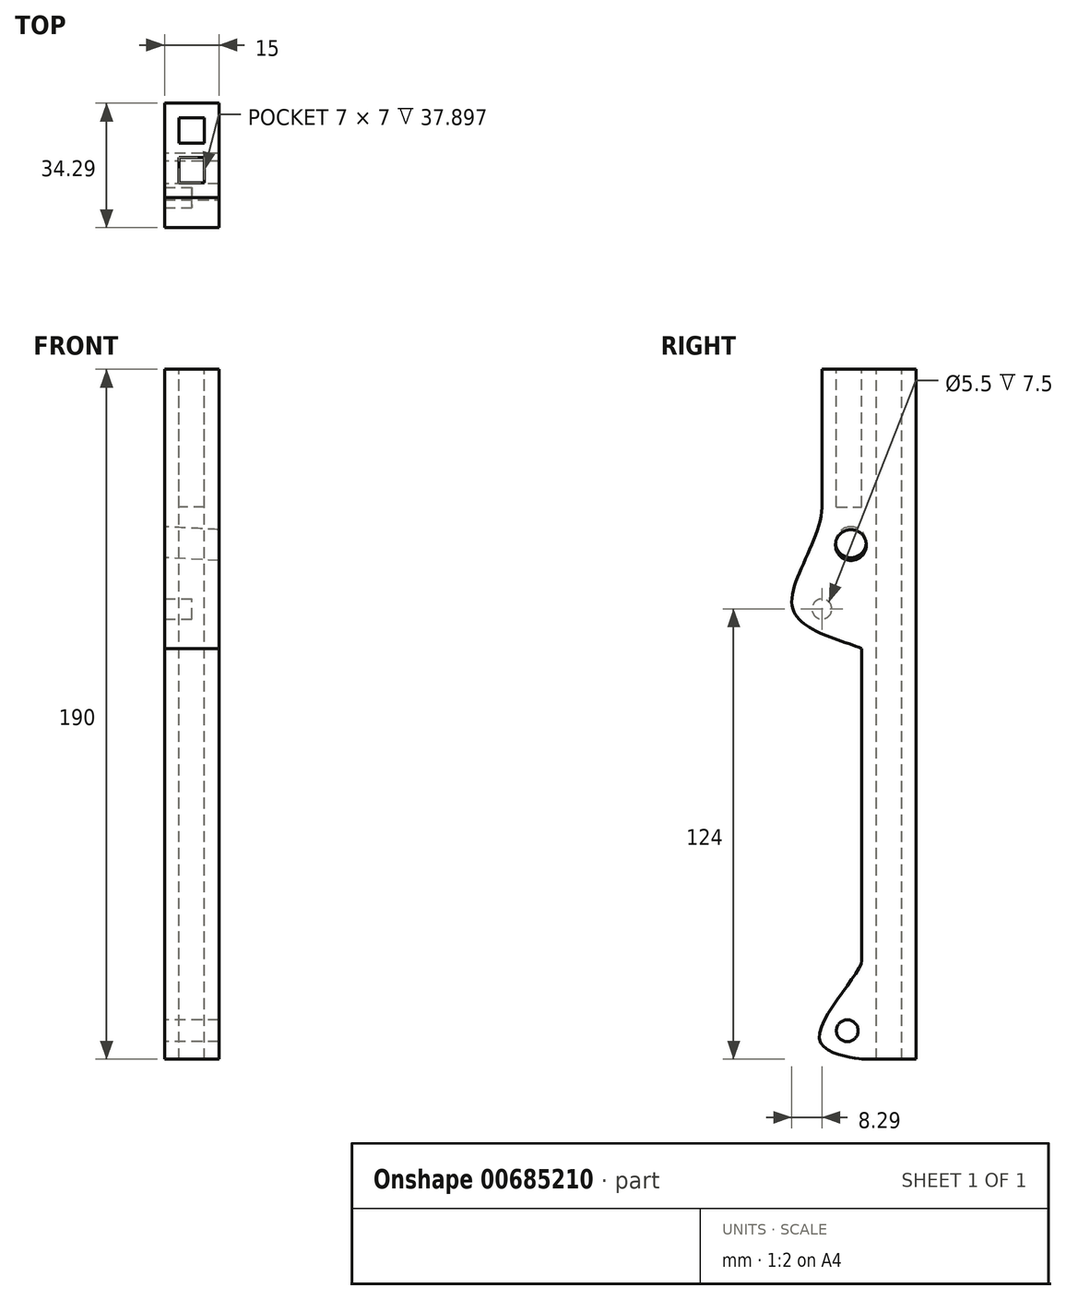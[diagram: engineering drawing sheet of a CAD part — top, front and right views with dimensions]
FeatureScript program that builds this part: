
annotation { "Feature Type Name" : "Feature", "Feature Type Description" : "" }
export const myFeature = defineFeature(function(context is Context, id is Id, definition is map)
    precondition{}
    {
        {
            var Q0;
            Q0=qCreatedBy(makeId("Right.planeOp"),FACE);
            var sketch = newSketch(context, id + "F0", { "sketchPlane" : qUnion([Q0])});
            skLineSegment(sketch, "E0.bottom", {"start": v(7.5, -95) * mm, "end": v(-7.5, -95) * mm});
            skLineSegment(sketch, "E0.top", {"start": v(7.5, 95) * mm, "end": v(-7.5, 95) * mm});
            skLineSegment(sketch, "E0.left", {"start": v(7.5, -95) * mm, "end": v(7.5, 95) * mm});
            skLineSegment(sketch, "E0.right", {"start": v(-7.5, -95) * mm, "end": v(-7.5, 95) * mm});
            skPoint(sketch, "E0.middle", {"position": v(0, 0) * mm});
            skSolve(sketch);
        }
        {
            var Q0;
            Q0=qSketchRegion(id+"F0",true);
            extrude(context, id + "F1", {"entities" : qUnion([Q0]), "endBound" : BoundingType.SYMMETRIC, "depth" : 15 * mm, "offsetDistance" : 25 * mm});
        }
        {
            var Q0;
            Q0=makeQuery(id+"F1.opExtrude","SWEPT_FACE",FACE,{"disambiguationData":[OSD([sQuery(id+"F0.wireOp",EDGE,"E0.top")])]});
            var sketch = newSketch(context, id + "F2", { "sketchPlane" : qUnion([Q0])});
            skLineSegment(sketch, "E1.bottom", {"start": v(3.5, 3.5) * mm, "end": v(-3.5, 3.5) * mm});
            skLineSegment(sketch, "E1.top", {"start": v(3.5, -3.5) * mm, "end": v(-3.5, -3.5) * mm});
            skLineSegment(sketch, "E1.left", {"start": v(3.5, 3.5) * mm, "end": v(3.5, -3.5) * mm});
            skLineSegment(sketch, "E1.right", {"start": v(-3.5, 3.5) * mm, "end": v(-3.5, -3.5) * mm});
            skPoint(sketch, "E1.middle", {"position": v(0, 0) * mm});
            skSolve(sketch);
        }
        {
            var Q0;
            Q0=qSketchRegion(id+"F2",true);
            extrude(context, id + "F3", {"entities" : qUnion([Q0]), "operationType" : NewBodyOperationType.REMOVE, "endBound" : BoundingType.THROUGH_ALL, "oppositeDirection" : true, "depth" : 25 * mm, "offsetDistance" : 25 * mm});
        }
        {
            var Q0;
            Q0=makeQuery(id+"F1.opExtrude","CAP_FACE",FACE,{"disambiguationData":[OSD([sQuery(id+"F0.wireOp",EDGE,"E0.bottom"),sQuery(id+"F0.wireOp",EDGE,"E0.top"),sQuery(id+"F0.wireOp",EDGE,"E0.left"),sQuery(id+"F0.wireOp",EDGE,"E0.right")])],"isStart":false});
            var sketch = newSketch(context, id + "F4", { "sketchPlane" : qUnion([Q0])});
            skLineSegment(sketch, "E2", {"start": v(-7.5, 95) * mm, "end": v(-18.5, 95) * mm});
            skLineSegment(sketch, "E3", {"start": v(-18.5, 95) * mm, "end": v(-18.5, 50) * mm});
            skLineSegment(sketch, "E4", {"start": v(-18.5, 50) * mm, "end": v(-7.5, 50) * mm});
            skSolve(sketch);
        }
        {
            var Q0;
            {var subQ0=sQuery(id+"F4.wireOp",EDGE,"E2");Q0=makeQuery(id+"F4.imprint","IMPRINT",FACE,{"disambiguationData":[TD([[makeQuery(id+"F4.imprint","IMPRINT",EDGE,{"derivedFrom":subQ0}),1.0]])]});}
            extrude(context, id + "F5", {"entities" : qUnion([Q0]), "operationType" : NewBodyOperationType.ADD, "oppositeDirection" : true, "depth" : 15 * mm, "offsetDistance" : 25 * mm});
        }
        {
            var Q0;
            Q0=makeQuery(id+"F5.boolean.opBoolean","MERGE",FACE,{"derivedFrom":[makeQuery(id+"F1.opExtrude","SWEPT_FACE",FACE,{"disambiguationData":[OSD([sQuery(id+"F0.wireOp",EDGE,"E0.top")])]}),makeQuery(id+"F5.opExtrude","SWEPT_FACE",FACE,{"disambiguationData":[OSD([sQuery(id+"F4.wireOp",EDGE,"E2")])]})]});
            var sketch = newSketch(context, id + "F6", { "sketchPlane" : qUnion([Q0])});
            skLineSegment(sketch, "E5", {"start": v(-3.5, -7.5) * mm, "end": v(3.5, -7.5) * mm});
            skLineSegment(sketch, "E6", {"start": v(3.5, -7.5) * mm, "end": v(3.5, -14.5) * mm});
            skLineSegment(sketch, "E7", {"start": v(3.5, -14.5) * mm, "end": v(-3.5, -14.5) * mm});
            skLineSegment(sketch, "E8", {"start": v(-3.5, -14.5) * mm, "end": v(-3.5, -7.5) * mm});
            skSolve(sketch);
        }
        {
            var Q0;
            Q0=makeQuery(id+"F6.imprint","IMPRINT",FACE,{"disambiguationData":[TD([[makeQuery(id+"F6.imprint","IMPRINT",EDGE,{"derivedFrom":sQuery(id+"F6.wireOp",EDGE,"E5")}),-1.0]])]});
            extrude(context, id + "F7", {"entities" : qUnion([Q0]), "operationType" : NewBodyOperationType.REMOVE, "oppositeDirection" : true, "depth" : 40 * mm, "offsetDistance" : 25 * mm});
        }
        {
            var Q0;
            Q0=qCreatedBy(makeId("Right.planeOp"),FACE);
            var sketch = newSketch(context, id + "F8", { "sketchPlane" : qUnion([Q0])});
            skPoint(sketch, "E9", {"position": v(-10.5, 47) * mm});
            skSolve(sketch);
        }
        {
            var Q0;
            Q0=qCreatedBy(makeId("Right.planeOp"),FACE);
            var sketch = newSketch(context, id + "F9", { "sketchPlane" : qUnion([Q0])});
            skPoint(sketch, "E10", {"position": v(-18.5, 29) * mm});
            skPoint(sketch, "E11", {"position": v(-7.5, 18.1) * mm});
            skLineSegment(sketch, "E12", {"start": v(-18.5, 29) * mm, "end": v(-26.5, 29) * mm});
            skFitSpline(sketch, "E13", {"points": [v(-18.5, 57.1) * mm, v(-26.5, 29) * mm, v(-7.5, 18.1) * mm], "startDerivative": vector(0.32, -51.24) * mm, "endDerivative": vector(40, -16.22) * mm});
            skLineSegment(sketch, "E14", {"start": v(-18.5, 57.1) * mm, "end": v(-7.5, 57.1) * mm});
            skLineSegment(sketch, "E15", {"start": v(-7.5, 18.1) * mm, "end": v(-7.5, 57.1) * mm});
            skSolve(sketch);
        }
        {
            var Q0;
            Q0=qSketchRegion(id+"F9",true);
            extrude(context, id + "F10", {"entities" : qUnion([Q0]), "endBound" : BoundingType.SYMMETRIC, "depth" : 15 * mm, "offsetDistance" : 25 * mm});
        }
        {
            var Q0;
            Q0=makeQuery(id+"F10.opExtrude","SWEPT_BODY",BODY,{"disambiguationData":[OSD([sQuery(id+"F9.wireOp",EDGE,"E13"),sQuery(id+"F9.wireOp",EDGE,"E14"),sQuery(id+"F9.wireOp",EDGE,"E15")])]});
            var Q1;
            Q1=makeQuery(id+"F1.opExtrude","SWEPT_BODY",BODY,{"disambiguationData":[OSD([sQuery(id+"F0.wireOp",EDGE,"E0.bottom"),sQuery(id+"F0.wireOp",EDGE,"E0.top"),sQuery(id+"F0.wireOp",EDGE,"E0.left"),sQuery(id+"F0.wireOp",EDGE,"E0.right")])]});
            booleanBodies(context, id + "F11", {"operationType" : BooleanOperationType.UNION, "tools" : qUnion([Q0, Q1])});
        }
        {
            var Q0;
            Q0=sQuery(id+"F9.wireOp",VERTEX,"E10");
            var Q1;
            Q1=makeQuery(id+"F10.opExtrude","SWEPT_BODY",BODY,{"disambiguationData":[OSD([sQuery(id+"F9.wireOp",EDGE,"E13"),sQuery(id+"F9.wireOp",EDGE,"E14"),sQuery(id+"F9.wireOp",EDGE,"E15")])]});
            hole(context, id + "F12", {"style" : HoleStyle.SIMPLE, "endStyle" : HoleEndStyle.BLIND, "standardTappedOrClearance" : lookupTablePath({ "standard" : "ISO", "fit" : "Normal", "size" : "M5", "type" : "Clearance" }), "standardBlindInLast" : lookupTablePath({ "fit" : "Standard", "standard" : "ISO", "size" : "M5", "type" : "Clearance" }), "holeDiameter" : 5.5 * mm, "majorDiameter" : 5 * mm, "holeDepth" : 12 * mm, "isTappedThrough" : true, "tappedDepth" : 12 * mm, "tapClearance" : 3, "locations" : qUnion([Q0]), "scope" : qUnion([Q1])});
        }
        {
            var Q0;
            Q0=qCreatedBy(makeId("Front.planeOp"),FACE);
            var Q1;
            Q1=makeQuery(id+"F1.opExtrude","SWEPT_EDGE",EDGE,{"disambiguationData":[OSD([sQuery(id+"F0.wireOp",EDGE,"E0.bottom"),sQuery(id+"F0.wireOp",EDGE,"E0.right")])]});
            cPlane(context, id + "F13", {"entities" : qUnion([Q0, Q1]), "cplaneType" : CPlaneType.LINE_ANGLE, "offset" : 40 * mm, "angle" : 70 * degree, "oppositeDirection" : true, "width" : 150 * mm, "height" : 150 * mm});
        }
        {
            var Q0;
            Q0=qCreatedBy(makeId("Right.planeOp"),FACE);
            var Q1;
            Q1=makeQuery(id+"F5.boolean.opBoolean","MERGE",EDGE,{"derivedFrom":[makeQuery(id+"F1.opExtrude","CAP_EDGE",EDGE,{"disambiguationData":[OSD([sQuery(id+"F0.wireOp",EDGE,"E0.top")])],"isStart":false}),makeQuery(id+"F5.opExtrude","CAP_EDGE",EDGE,{"disambiguationData":[OSD([sQuery(id+"F4.wireOp",EDGE,"E2")])],"isStart":true})]});
            cPlane(context, id + "F14", {"entities" : qUnion([Q0, Q1]), "cplaneType" : CPlaneType.LINE_ANGLE, "offset" : 25 * mm, "angle" : 3 * degree, "oppositeDirection" : true, "width" : 150 * mm, "height" : 150 * mm});
        }
        {
            var Q0;
            Q0=qCreatedBy(id+"F14.planeOp",FACE);
            var sketch = newSketch(context, id + "F15", { "sketchPlane" : qUnion([Q0])});
            skCircle(sketch, "E16", {"center": v(10.5, 46.94) * mm, "radius": 4.25 * mm});
            skSolve(sketch);
        }
        {
            var Q0;
            Q0=qSketchRegion(id+"F15",true);
            extrude(context, id + "F16", {"entities" : qUnion([Q0]), "operationType" : NewBodyOperationType.REMOVE, "endBound" : BoundingType.SYMMETRIC, "oppositeDirection" : true, "depth" : 50 * mm, "offsetDistance" : 25 * mm});
        }
        {
            var Q0;
            Q0=qCreatedBy(makeId("Right.planeOp"),FACE);
            var sketch = newSketch(context, id + "F17", { "sketchPlane" : qUnion([Q0])});
            skPoint(sketch, "E17", {"position": v(-7.5, -95) * mm});
            skFitSpline(sketch, "E18", {"points": [v(-7.5, -95) * mm, v(-19.06, -89.77) * mm, v(-7.5, -67.81) * mm], "startDerivative": vector(-14.27, 3.2) * mm, "endDerivative": vector(-0.08, 18.34) * mm});
            skCircle(sketch, "E19", {"center": v(-11.5, -87.16) * mm, "radius": 3 * mm});
            skLineSegment(sketch, "E20", {"start": v(-7.5, -67.81) * mm, "end": v(-7.5, -95) * mm});
            skSolve(sketch);
        }
        {
            var Q0;
            Q0=qSketchRegion(id+"F17",true);
            extrude(context, id + "F18", {"entities" : qUnion([Q0]), "operationType" : NewBodyOperationType.ADD, "endBound" : BoundingType.SYMMETRIC, "depth" : 15 * mm, "offsetDistance" : 25 * mm});
        }
    });
